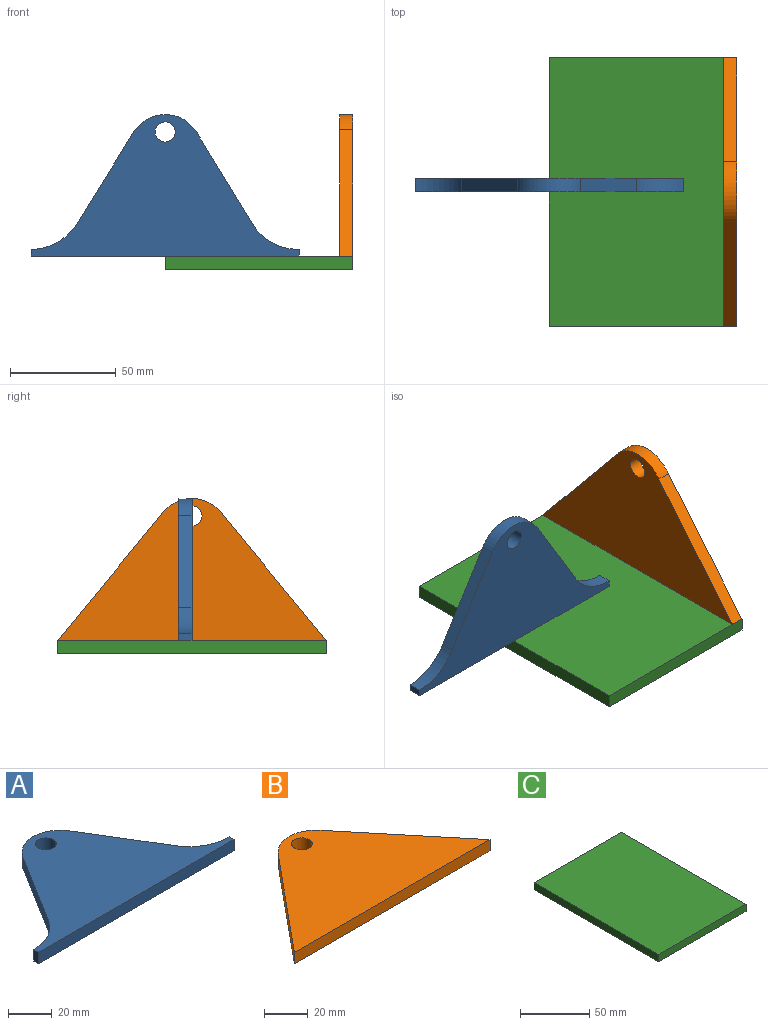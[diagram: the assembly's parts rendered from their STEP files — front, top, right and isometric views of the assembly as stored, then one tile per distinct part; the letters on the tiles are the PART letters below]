
ASSEMBLY  parts=3 mates=2
PART A: 11 faces, bbox 127x67x6.4 mm
  f0: plane 6.35x3.18mm, normal (-1,0,0), area 20.2mm2, adj f1,f8,f9,f10
  f1: plane 127x6.35mm, normal (0,-1,0), area 806.5mm2, adj f0,f2,f9,f10
  f2: plane 6.35x3.18mm, normal (1,0,0), area 20.2mm2, adj f1,f3,f9,f10
  f3: cylinder r=25.4mm len=22.24mm, axis (0,0,-1), area 168.6mm2, adj f2,f4,f9,f10
  f4: plane 43.38x26.43mm, normal (0.85,0.52,0), area 322.6mm2, adj f3,f5,f9,f10
  f5: cylinder r=17.46mm len=29.65mm, axis (0,0,-1), area 224.9mm2, adj f4,f6,f9,f10
  f6: plane 43.13x26.83mm, normal (-0.85,0.53,0), area 322.6mm2, adj f5,f8,f9,f10
  f7: cylinder r=4.76mm len=9.53mm, axis (0,0,-1), area 190mm2, adj f9,f10
  f8: cylinder r=25.4mm len=21.84mm, axis (0,0,-1), area 166.9mm2, adj f0,f6,f9,f10
  f9: plane 127x66.98mm, normal (0,0,1), area 4116.2mm2, adj f0,f1,f2,f3,f4,f5,f6,f7
  f10: plane 127x66.98mm, normal (0,0,-1), area 4116.2mm2, adj f0,f1,f2,f3,f4,f5,f6,f7
PART B: 7 faces, bbox 127x67x6.4 mm
  f0: plane 59.68x49.3mm, normal (0.77,0.64,0), area 491.5mm2, adj f1,f3,f5,f6
  f1: cylinder r=17.46mm len=28.4mm, axis (0,0,-1), area 210.6mm2, adj f0,f2,f5,f6
  f2: plane 59.68x49.3mm, normal (-0.77,0.64,0), area 491.5mm2, adj f1,f3,f5,f6
  f3: plane 127x6.35mm, normal (0,-1,0), area 806.5mm2, adj f0,f2,f5,f6
  f4: cylinder r=4.76mm len=9.53mm, axis (0,0,-1), area 190mm2, adj f5,f6
  f5: plane 127x66.98mm, normal (0,0,1), area 4711.2mm2, adj f0,f1,f2,f3,f4
  f6: plane 127x66.98mm, normal (0,0,-1), area 4711.2mm2, adj f0,f1,f2,f3,f4
PART C: 6 faces, bbox 88.9x127x6.4 mm
  f0: plane 127x6.35mm, normal (-1,0,0), area 806.5mm2, adj f1,f3,f4,f5
  f1: plane 88.9x6.35mm, normal (0,-1,0), area 564.5mm2, adj f0,f2,f4,f5
  f2: plane 127x6.35mm, normal (1,0,0), area 806.5mm2, adj f1,f3,f4,f5
  f3: plane 88.9x6.35mm, normal (0,1,0), area 564.5mm2, adj f0,f2,f4,f5
  f4: plane 127x88.9mm, normal (0,0,1), area 11290.3mm2, adj f0,f1,f2,f3
  f5: plane 127x88.9mm, normal (0,0,-1), area 11290.3mm2, adj f0,f1,f2,f3
PLACE A rot(axis=(1,0,0),90deg) t=(-47.96,54.22,23.03)mm
PLACE B rot(axis=(0.58,-0.58,-0.58),120deg) t=(104.44,111.37,23.03)mm
PLACE C t=(15.54,-15.63,16.68)mm
MATE fastened A.f1 <-> C.f4  axis (0,0,-1) through (15.54,47.87,23.03)mm
MATE fastened B.f3 <-> C.f4  axis (0,0,-1) through (104.44,47.87,23.03)mm
